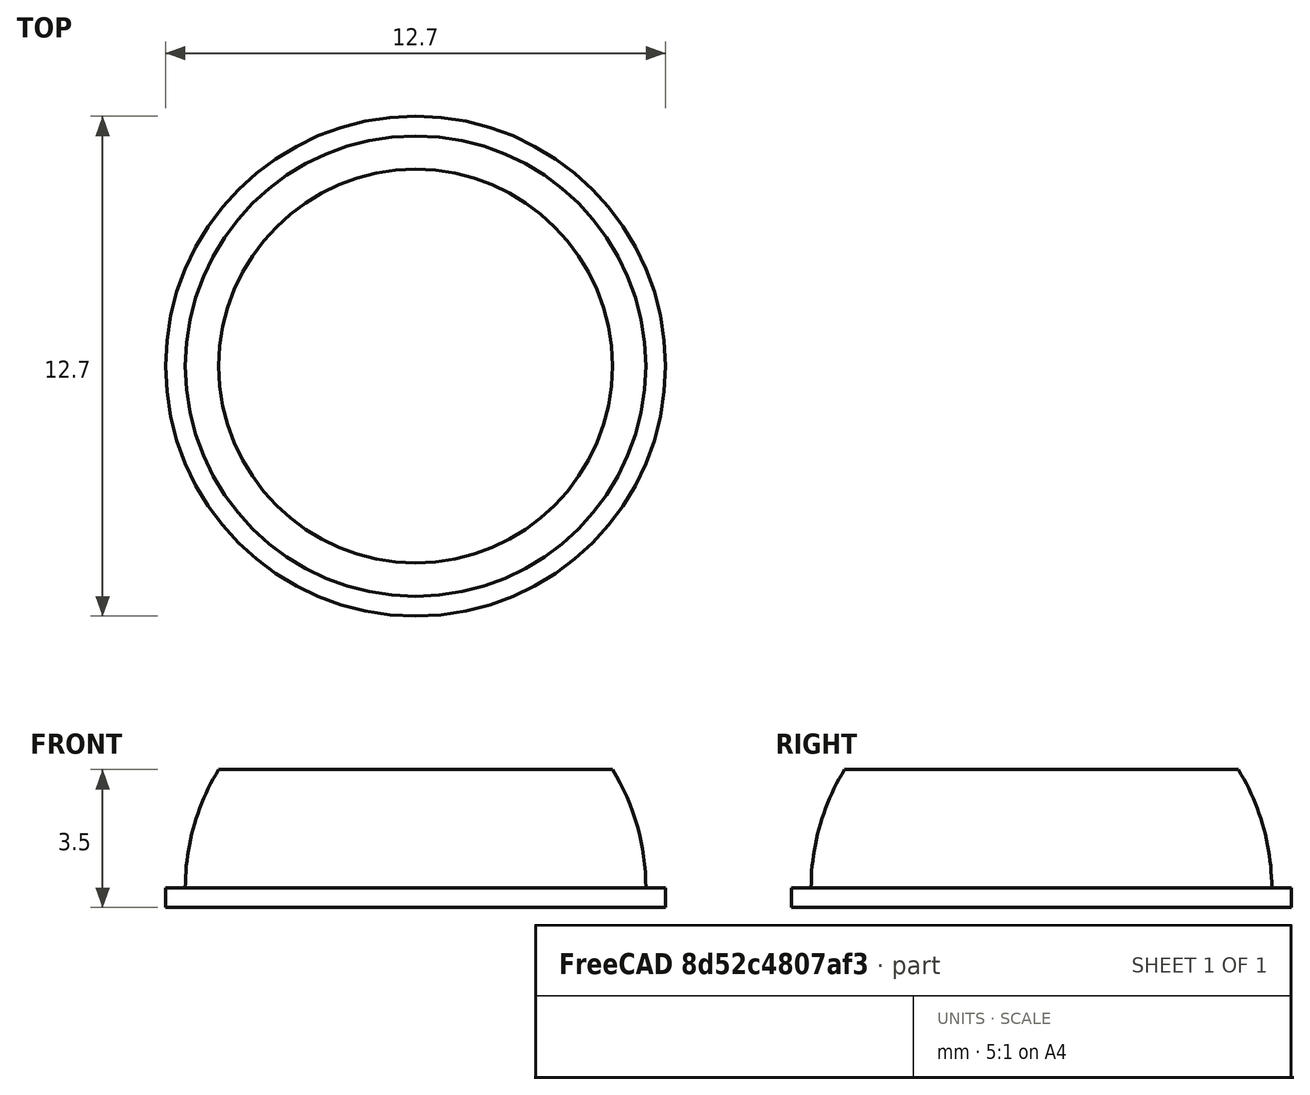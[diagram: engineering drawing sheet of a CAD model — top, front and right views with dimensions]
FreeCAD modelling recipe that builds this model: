
FCSTD DOCUMENT  (FreeCAD 2024.2R37240 (Git))
Label: 3M_bumpon_SJ5312
License: All rights reserved
LicenseURL: https://en.wikipedia.org/wiki/All_rights_reserved
objects: Sketcher::SketchObject×1, PartDesign::Revolution×1, PartDesign::CoordinateSystem×1, PartDesign::Body×1
note: 5 computed .brp shape members not serialized (recipe doc carries the construction recipe); baked Part::Feature solids carry a one-line shape summary decoded from their .brp

FEATURE [Sketcher::SketchObject] Sketch
  AttachmentSupport = -> [XZ_Plane]
  FullyConstrained = true
  MapMode = 5
  Placement = pos=(0,0,0) rot=(1,0,0;1.5708rad)
  sketch-geometry (6):
    g0: LineSegment StartX=0 StartY=0 StartZ=0 EndX=0 EndY=3.5 EndZ=0
    g1: LineSegment StartX=0 StartY=3.5 StartZ=0 EndX=5 EndY=3.5 EndZ=0
    g2: ArcOfCircle CenterX=0.130882 CenterY=0.5 CenterZ=0 NormalX=0 NormalY=0 NormalZ=1 AngleXU=0 Radius=5.71912 StartAngle=0 EndAngle=0.552194
    g3: LineSegment StartX=0 StartY=0 StartZ=0 EndX=6.35 EndY=0 EndZ=0
    g4: LineSegment StartX=6.35 StartY=0 StartZ=0 EndX=6.35 EndY=0.5 EndZ=0
    g5: LineSegment StartX=6.35 StartY=0.5 StartZ=0 EndX=5.85 EndY=0.5 EndZ=0
  constraints (18):
    c: Coincident(g-1,g0)
    c: PointOnObject(g0,g-2)
    c: DistanceY(g0,g0) = 3.5
    c: Coincident(g0,g1)
    c: Horizontal(g1)
    c: Coincident(g2,g1)
    c: Coincident(g0,g3)
    c: PointOnObject(g3,g-1)
    c: Coincident(g3,g4)
    c: Coincident(g4,g5)
    c: Coincident(g5,g2)
    c: Horizontal(g5)
    c: Vertical(g4)
    c: DistanceX(g3,g3) = 6.35
    c: DistanceY(g4,g4) = 0.5
    c: Equal(g5,g4)
    c: Perpendicular(g2,g5)
    c: DistanceX(g1,g1) = 5
FEATURE [PartDesign::Revolution] Revolution
  Angle = 360
  Angle2 = 60
  Axis = (0,2e-16,1)
  Base = (0,0,0)
  Placement = pos=(0,0,0) rot=(1,0,0;1.5708rad)
  Profile = -> Sketch
  ReferenceAxis = -> Sketch [V_Axis]
  Refine = true
  Reversed = true
  Suppressed = false
  Type = 0
FEATURE [PartDesign::CoordinateSystem] mounting_surface  label="mounting-surface"
  AttacherType = Attacher::AttachEngine3D
  AttachmentSupport = -> [Revolution]
  MapMode = 45
  Placement = pos=(1.8e-15,1.1e-15,0) rot=(0,1,0;3.14159rad)
FEATURE [PartDesign::Body] Body  label="bumpon"
  Group = -> [Sketch,Revolution,mounting_surface]
  Origin = -> Origin
  Tip = -> Revolution
